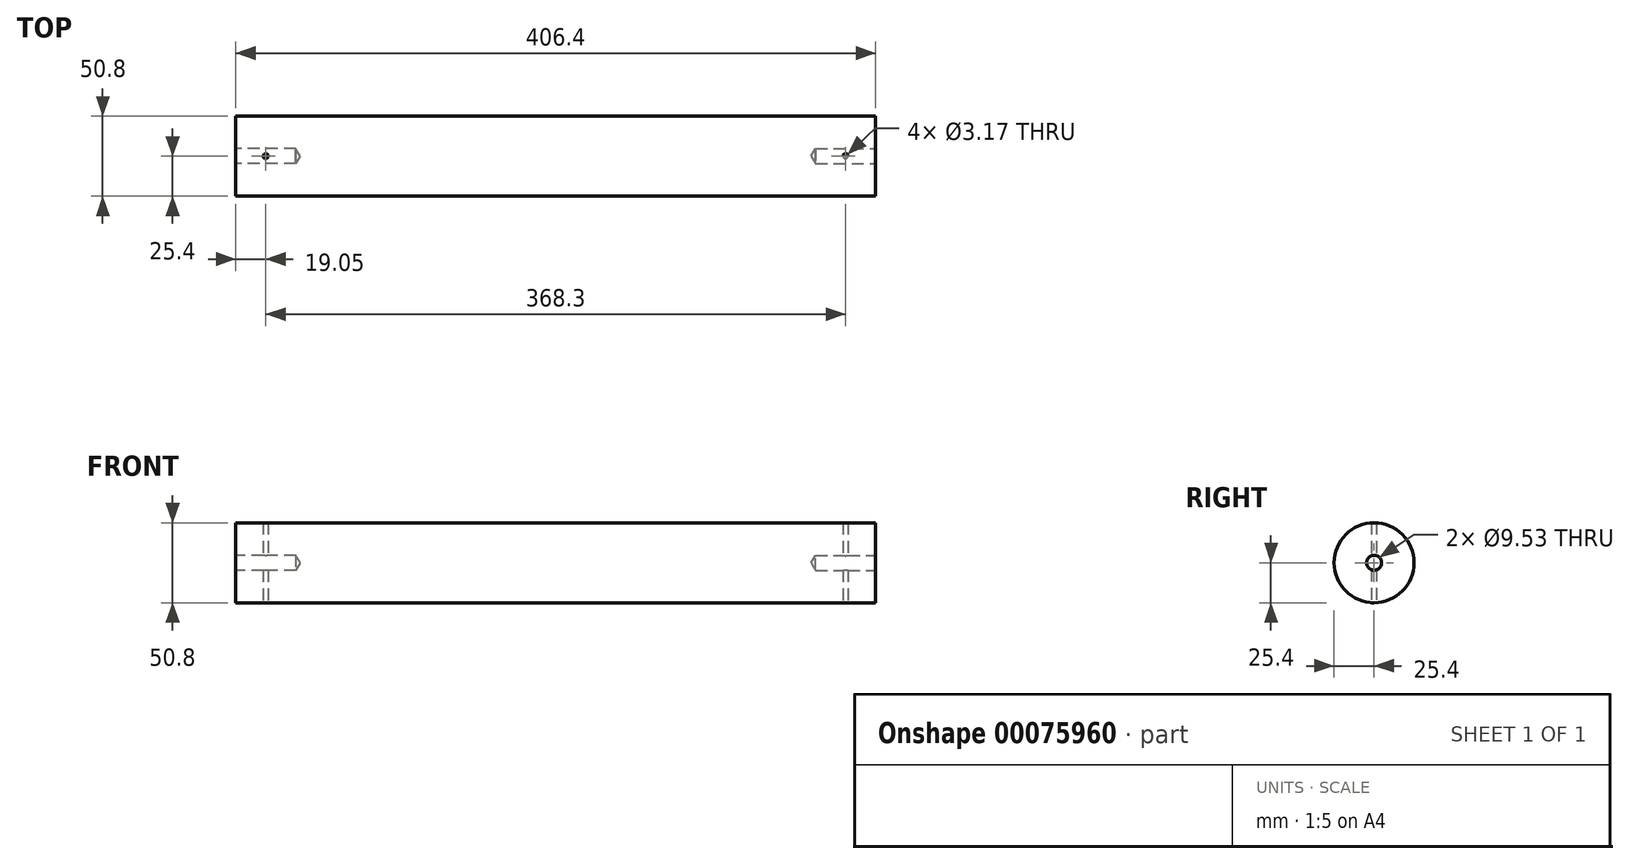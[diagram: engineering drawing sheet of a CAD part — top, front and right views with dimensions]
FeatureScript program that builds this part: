
annotation { "Feature Type Name" : "Feature", "Feature Type Description" : "" }
export const myFeature = defineFeature(function(context is Context, id is Id, definition is map)
    precondition{}
    {
        {
            var Q0;
            Q0=qCreatedBy(makeId("Right.planeOp"),FACE);
            var sketch = newSketch(context, id + "F0", { "sketchPlane" : qUnion([Q0])});
            skCircle(sketch, "E0", {"center": v(0, 0) * mm, "radius": 25.4 * mm});
            skSolve(sketch);
        }
        {
            var Q0;
            Q0=makeQuery(id+"F0.imprint","IMPRINT",FACE,{"disambiguationData":[TD([[makeQuery(id+"F0.imprint","IMPRINT",EDGE,{"derivedFrom":sQuery(id+"F0.wireOp",EDGE,"E0")}),1.0]])]});
            extrude(context, id + "F1", {"entities" : qUnion([Q0]), "depth" : 406.4 * mm});
        }
        {
            var Q0;
            Q0=makeQuery(id+"F1.opExtrude","CAP_FACE",FACE,{"disambiguationData":[OSD([sQuery(id+"F0.wireOp",EDGE,"E0")])],"isStart":false});
            var sketch = newSketch(context, id + "F2", { "sketchPlane" : qUnion([Q0])});
            skPoint(sketch, "E1", {"position": v(0, 0) * mm});
            skSolve(sketch);
        }
        {
            var Q0;
            Q0=sQuery(id+"F2.wireOp",VERTEX,"E1");
            var Q1;
            Q1=makeQuery(id+"F1.opExtrude","SWEPT_BODY",BODY,{"disambiguationData":[OSD([sQuery(id+"F0.wireOp",EDGE,"E0")])]});
            hole(context, id + "F3", {"style" : HoleStyle.SIMPLE, "endStyle" : HoleEndStyle.BLIND, "holeDiameter" : 9.52 * mm, "holeDepth" : 38.1 * mm, "locations" : qUnion([Q0]), "scope" : qUnion([Q1])});
        }
        {
            var Q0;
            Q0=makeQuery(id+"F1.opExtrude","CAP_FACE",FACE,{"disambiguationData":[OSD([sQuery(id+"F0.wireOp",EDGE,"E0")])],"isStart":true});
            var sketch = newSketch(context, id + "F4", { "sketchPlane" : qUnion([Q0])});
            skPoint(sketch, "E2", {"position": v(0, 0) * mm});
            skSolve(sketch);
        }
        {
            var Q0;
            Q0=sQuery(id+"F4.wireOp",VERTEX,"E2");
            var Q1;
            Q1=makeQuery(id+"F1.opExtrude","SWEPT_BODY",BODY,{"disambiguationData":[OSD([sQuery(id+"F0.wireOp",EDGE,"E0")])]});
            hole(context, id + "F5", {"style" : HoleStyle.SIMPLE, "endStyle" : HoleEndStyle.BLIND, "holeDiameter" : 9.52 * mm, "holeDepth" : 38.1 * mm, "locations" : qUnion([Q0]), "scope" : qUnion([Q1])});
        }
        {
            var Q0;
            Q0=qCreatedBy(makeId("Top.planeOp"),FACE);
            var sketch = newSketch(context, id + "F6", { "sketchPlane" : qUnion([Q0])});
            skCircle(sketch, "E3", {"center": v(19.05, 0) * mm, "radius": 1.59 * mm});
            skCircle(sketch, "E4", {"center": v(387.35, 0) * mm, "radius": 1.59 * mm});
            skSolve(sketch);
        }
        {
            var Q0;
            Q0=makeQuery(id+"F6.imprint","IMPRINT",FACE,{"disambiguationData":[TD([[makeQuery(id+"F6.imprint","IMPRINT",EDGE,{"derivedFrom":sQuery(id+"F6.wireOp",EDGE,"E3")}),1.0]])]});
            extrude(context, id + "F7", {"entities" : qUnion([Q0]), "endBound" : BoundingType.SYMMETRIC, "depth" : 50.8 * mm});
        }
        {
            var Q0;
            Q0=makeQuery(id+"F7.opExtrude","SWEPT_BODY",BODY,{"disambiguationData":[OSD([sQuery(id+"F6.wireOp",EDGE,"E3")])]});
            var Q1;
            Q1=makeQuery(id+"F1.opExtrude","SWEPT_BODY",BODY,{"disambiguationData":[OSD([sQuery(id+"F0.wireOp",EDGE,"E0")])]});
            booleanBodies(context, id + "F8", {"operationType" : BooleanOperationType.SUBTRACTION, "tools" : qUnion([Q0]), "targets" : qUnion([Q1])});
        }
        {
            var Q0;
            Q0=makeQuery(id+"F6.imprint","IMPRINT",FACE,{"disambiguationData":[TD([[makeQuery(id+"F6.imprint","IMPRINT",EDGE,{"derivedFrom":sQuery(id+"F6.wireOp",EDGE,"E4")}),1.0]])]});
            extrude(context, id + "F9", {"entities" : qUnion([Q0]), "endBound" : BoundingType.SYMMETRIC, "depth" : 63.5 * mm});
        }
        {
            var Q0;
            Q0=makeQuery(id+"F9.opExtrude","SWEPT_BODY",BODY,{"disambiguationData":[OSD([sQuery(id+"F6.wireOp",EDGE,"E4")])]});
            var Q1;
            Q1=makeQuery(id+"F1.opExtrude","SWEPT_BODY",BODY,{"disambiguationData":[OSD([sQuery(id+"F0.wireOp",EDGE,"E0")])]});
            booleanBodies(context, id + "F10", {"operationType" : BooleanOperationType.SUBTRACTION, "tools" : qUnion([Q0]), "targets" : qUnion([Q1])});
        }
    });
